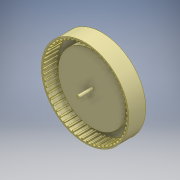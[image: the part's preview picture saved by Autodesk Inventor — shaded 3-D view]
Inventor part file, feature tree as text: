
AUTODESK INVENTOR PART (.ipt)
format: ipt  version: 2016 (Build 200138000, 138)  size: 347,648 bytes
history: native  units: mm
features: extrude x7, sketch x7, other x1, pattern_circular x1
ambient origin geometry x8: Origin, YZ Plane, XZ Plane, XY Plane, X Axis, Y Axis, Z Axis, Center Point
bodies: Body1 (feature_tree)
feature tree (16):
  other  "Sólido1"
  extrude  "Extrusión1"  Depth=2.0mm TaperAngle=0.0deg
  extrude  "Extrusión2"  Depth=60.0mm
  extrude  "Extrusión3"  Depth=10.0mm TaperAngle=0.0deg
  pattern_circular  "Patrón circular1"  Count=55 Angle=360.0deg
  extrude  "Extrusión5"  Depth=2.0mm
  extrude  "Extrusión6"  Depth=15.0mm TaperAngle=0.0deg
  extrude  "Extrusión7"  Depth=2.0mm
  extrude  "Extrusión8"  Depth=5.0mm TaperAngle=0.0deg
  sketch  "Boceto1"  dims[d0=62.0mm d1=2.0mm d2=0.0mm]
  sketch  "Boceto2"  dims[d3=62.0mm d4=60.0mm]
  sketch  "Boceto4"  dims[d5=2.0mm d6=10.0mm d7=0.0mm]
  sketch  "Boceto6"  dims[d8=1.0mm]
  sketch  "Boceto7"  dims[d9=1.0mm]
  sketch  "Boceto8"  dims[d10=10.0mm d11=0.0mm d12=550.0mm d13=360.0deg]
  sketch  "Boceto9"  dims[d18=19.198622mm d20=12.217305mm d26=2.0mm d27=15.0mm d28=0.0mm d29=48.0mm d30=5.0mm d31=0.0mm d32=46.0mm d33=3.0mm d34=0.0mm d35=46.0mm d36=46.0mm d37=2.0mm d38=0.0mm]
